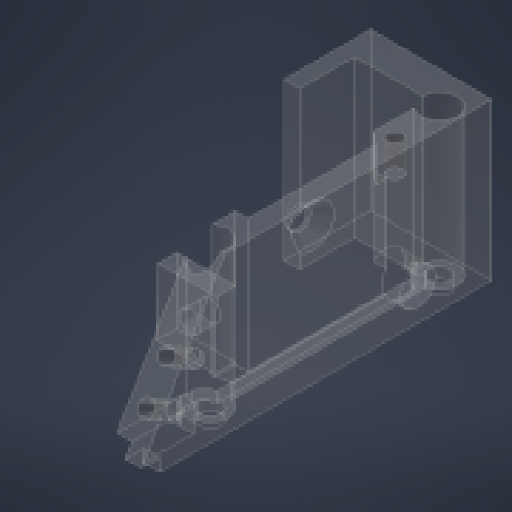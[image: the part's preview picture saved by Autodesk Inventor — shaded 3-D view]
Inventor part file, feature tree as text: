
AUTODESK INVENTOR PART (.ipt)
format: ipt  version: 2023 (Build 270158000, 158)  size: 323,072 bytes
history: native  units: mm
features: sketch x10, extrude x7, hole x5, other x1, fillet x1, chamfer x1
ambient origin geometry x8: Origin, YZ Plane, XZ Plane, XY Plane, X Axis, Y Axis, Z Axis, Center Point
bodies: Body1 (feature_tree)
feature tree (25):
  other  "Bryła1"
  extrude  "Wyciągnięcie proste1"  Depth=58.2mm
  extrude  "Wyciągnięcie proste2"  Depth=5.0mm
  extrude  "Wyciągnięcie proste3"  Depth=19.35mm
  hole  "Otwór1"  [1 undecoded]
  hole  "Otwór2"  [1 undecoded]
  hole  "Otwór4"  [1 undecoded]
  hole  "Otwór3"  [1 undecoded]
  sketch  "Szkic9"
  extrude  "Wyciągnięcie proste5"  Depth=5.2mm
  extrude  "Wyciągnięcie proste7"  Depth=2.0mm
  sketch  "Szkic10"
  extrude  "Wyciągnięcie proste8"  Depth=2.0mm
  hole  "Otwór5"  [1 undecoded]
  extrude  "Wyciągnięcie proste6"  Depth=2.5mm TaperAngle=0.0deg
  fillet  "Zaokrąglenie2"  Radius=4.2mm
  chamfer  "Faza1"  Distance=10.5mm
  sketch  "Szkic1"
  sketch  "Szkic2"
  sketch  "Szkic3"
  sketch  "Szkic4"
  sketch  "Szkic5"
  sketch  "Szkic6"
  sketch  "Szkic8"
  sketch  "Szkic11"
note: 5 required parameter values undecoded (feature->parameter linkage not recoverable at this tier; creation-order binding heuristic only, values carry confidence <= 0.55)
